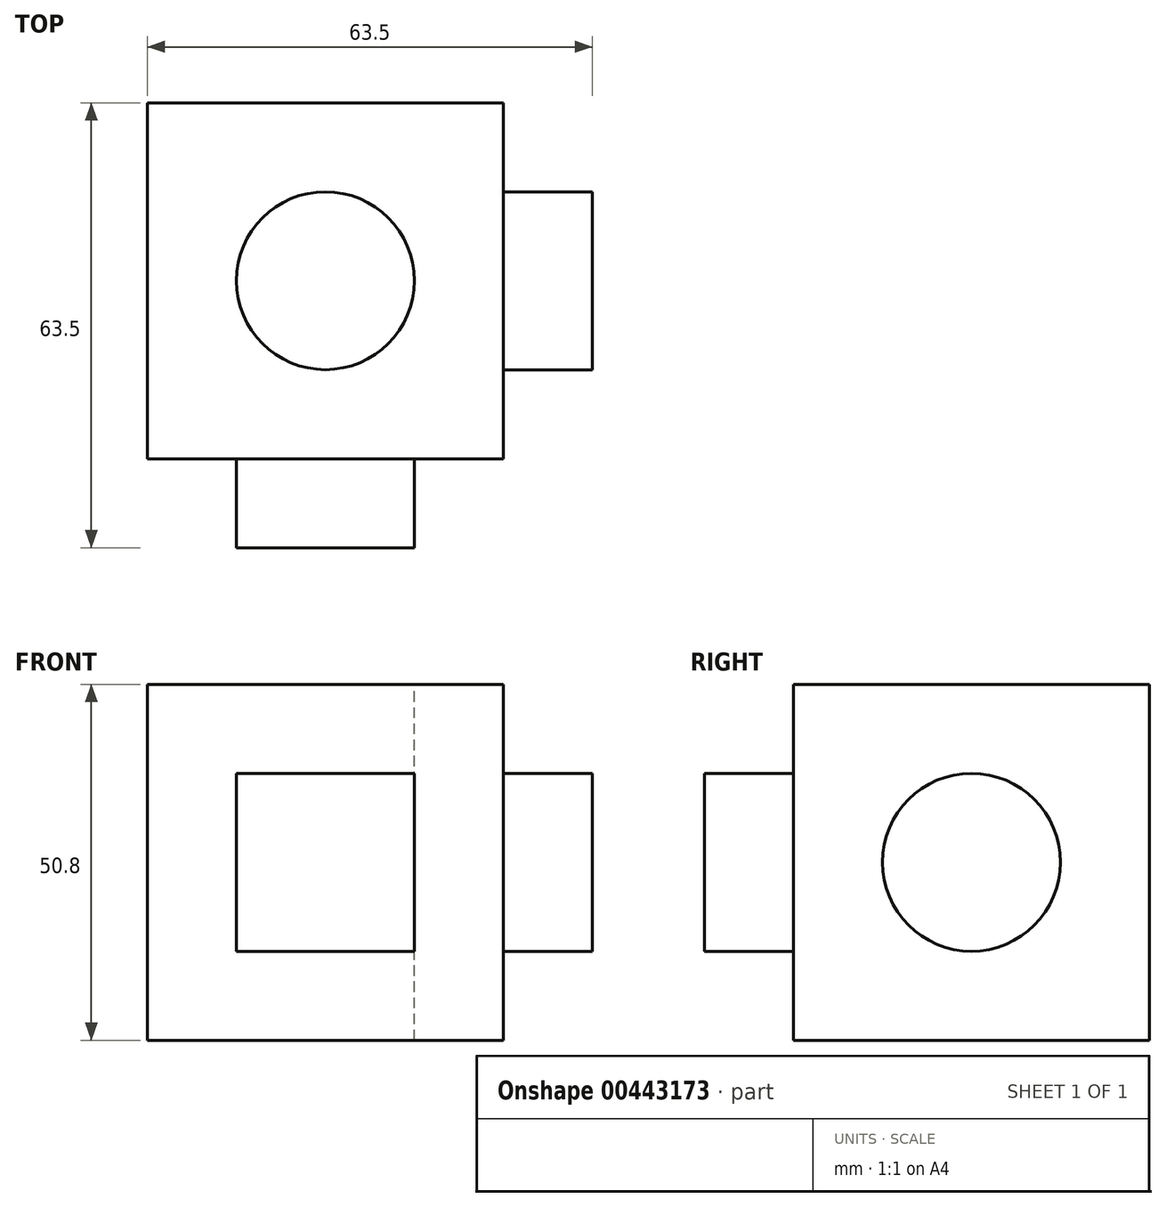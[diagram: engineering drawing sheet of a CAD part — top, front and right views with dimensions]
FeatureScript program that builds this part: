
annotation { "Feature Type Name" : "Feature", "Feature Type Description" : "" }
export const myFeature = defineFeature(function(context is Context, id is Id, definition is map)
    precondition{}
    {
        {
            var Q0;
            Q0=qCreatedBy(makeId("Front.planeOp"),FACE);
            var sketch = newSketch(context, id + "F0", { "sketchPlane" : qUnion([Q0])});
            skLineSegment(sketch, "E0", {"start": v(-50.8, 17.57) * mm, "end": v(-50.8, -33.23) * mm});
            skLineSegment(sketch, "E1", {"start": v(-50.8, -33.23) * mm, "end": v(0, -33.23) * mm});
            skLineSegment(sketch, "E2", {"start": v(0, -33.23) * mm, "end": v(0, 17.57) * mm});
            skLineSegment(sketch, "E3", {"start": v(0, 17.57) * mm, "end": v(-50.8, 17.57) * mm});
            skSolve(sketch);
        }
        {
            var Q0;
            Q0 = qSketchRegion(id + "F0", true);
            extrude(context, id + "F1", {"entities" : qUnion([Q0]), "depth" : 50.8 * mm});
        }
        {
            var Q0;
            Q0=makeQuery(id+"F1.opExtrude","SWEPT_FACE",FACE,{"disambiguationData":[OSD([sQuery(id+"F0.wireOp",EDGE,"E3")])]});
            var sketch = newSketch(context, id + "F2", { "sketchPlane" : qUnion([Q0])});
            skCircle(sketch, "E4", {"center": v(-25.4, -25.4) * mm, "radius": 12.7 * mm});
            skSolve(sketch);
        }
        {
            var Q0;
            Q0=makeQuery(id+"F2.imprint","IMPRINT",FACE,{"disambiguationData":[TD([[makeQuery(id+"F2.imprint","IMPRINT",EDGE,{"derivedFrom":sQuery(id+"F2.wireOp",EDGE,"E4")}),1.0]])]});
            extrude(context, id + "F3", {"entities" : qUnion([Q0]), "operationType" : NewBodyOperationType.REMOVE, "oppositeDirection" : true, "depth" : 101.6 * mm});
        }
        {
            var Q0;
            Q0=makeQuery(id+"F1.opExtrude","SWEPT_FACE",FACE,{"disambiguationData":[OSD([sQuery(id+"F0.wireOp",EDGE,"E2")])]});
            var sketch = newSketch(context, id + "F4", { "sketchPlane" : qUnion([Q0])});
            skCircle(sketch, "E5", {"center": v(-25.4, -7.83) * mm, "radius": 12.7 * mm});
            skSolve(sketch);
        }
        {
            var Q0;
            Q0=makeQuery(id+"F4.imprint","IMPRINT",FACE,{"disambiguationData":[TD([[makeQuery(id+"F4.imprint","IMPRINT",EDGE,{"derivedFrom":sQuery(id+"F4.wireOp",EDGE,"E5")}),1.0]])]});
            extrude(context, id + "F5", {"entities" : qUnion([Q0]), "operationType" : NewBodyOperationType.ADD, "depth" : 12.7 * mm});
        }
        {
            var Q0;
            Q0=makeQuery(id+"F1.opExtrude","CAP_FACE",FACE,{"disambiguationData":[OSD([sQuery(id+"F0.wireOp",EDGE,"E0"),sQuery(id+"F0.wireOp",EDGE,"E1"),sQuery(id+"F0.wireOp",EDGE,"E2"),sQuery(id+"F0.wireOp",EDGE,"E3")])],"isStart":false});
            var sketch = newSketch(context, id + "F6", { "sketchPlane" : qUnion([Q0])});
            skSolve(sketch);
        }
        {
            var Q0;
            Q0=makeQuery(id+"F6.imprint","IMPRINT",FACE,{"disambiguationData":[TD([[makeQuery(id+"F6.imprint","IMPRINT",EDGE,{"derivedFrom":makeQuery(id+"F1.opExtrude","CAP_EDGE",EDGE,{"disambiguationData":[OSD([sQuery(id+"F0.wireOp",EDGE,"E0")])],"isStart":false})}),1.0]])]});
            var sketch = newSketch(context, id + "F7", { "sketchPlane" : qUnion([Q0])});
            skLineSegment(sketch, "E6.bottom", {"start": v(-38.1, 4.87) * mm, "end": v(-12.7, 4.87) * mm});
            skLineSegment(sketch, "E6.top", {"start": v(-38.1, -20.53) * mm, "end": v(-12.7, -20.53) * mm});
            skLineSegment(sketch, "E6.left", {"start": v(-38.1, 4.87) * mm, "end": v(-38.1, -20.53) * mm});
            skLineSegment(sketch, "E6.right", {"start": v(-12.7, 4.87) * mm, "end": v(-12.7, -20.53) * mm});
            skSolve(sketch);
        }
        {
            var Q0;
            Q0 = qSketchRegion(id + "F7", true);
            extrude(context, id + "F8", {"entities" : qUnion([Q0]), "operationType" : NewBodyOperationType.ADD, "depth" : 12.7 * mm});
        }
    });
